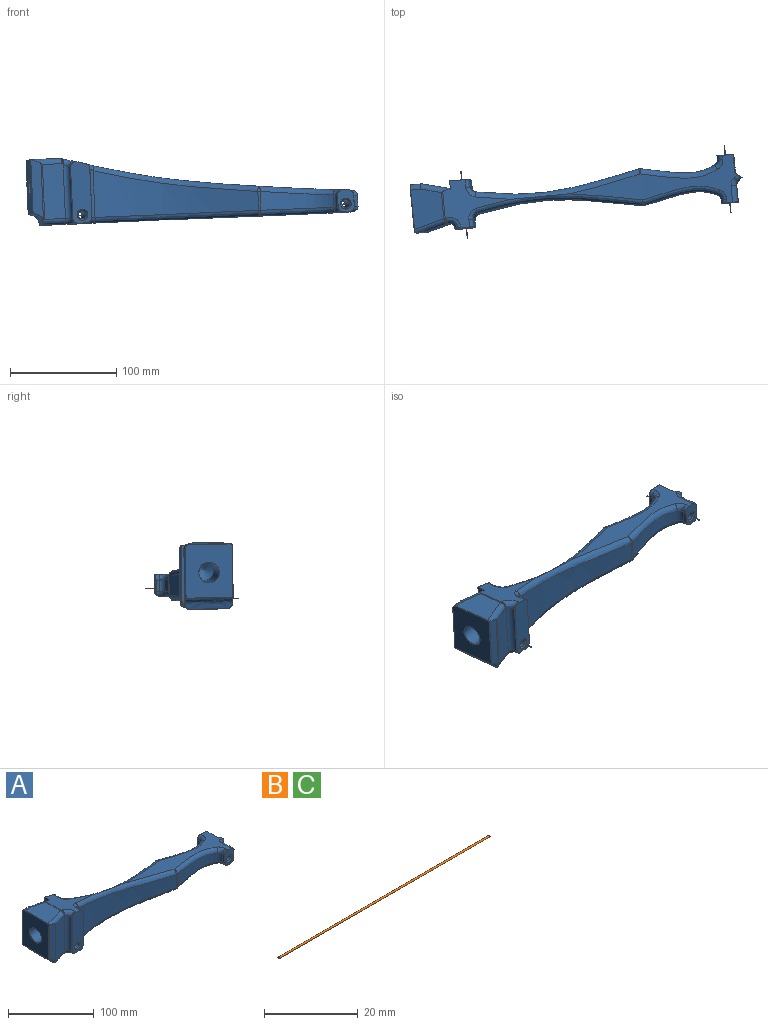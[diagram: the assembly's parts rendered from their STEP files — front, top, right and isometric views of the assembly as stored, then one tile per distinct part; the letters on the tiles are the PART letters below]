
ASSEMBLY  parts=3 mates=2
PART A: 137 faces, bbox 318.6x51.8x64.5 mm
  f0: bspline ~248.2x45mm, area 2358.8mm2, adj f35,f36,f41,f49,f51,f52,f54,f111
  f1: plane 155.5x39.82mm, normal (0,0,-1), area 2133.1mm2, adj f37,f46,f47,f48,f58,f92,f93,f94
  f2: plane 58.05x18.06mm, normal (0,-1,0), area 926.9mm2, adj f61,f62,f63,f64,f65,f66,f67,f68
  f3: plane 80.69x39.82mm, normal (0,0,-1), area 1452.2mm2, adj f37,f38,f40,f61,f74,f76,f77,f88
  f4: bspline ~218.34x45mm, area 1106.4mm2, adj f23,f41,f43,f44,f65,f70,f71,f73
  f5: plane 16.03x15.25mm, normal (0,1,0), area 166.9mm2, adj f96,f126,f128,f129,f130,f131
  f6: plane 54.56x18.06mm, normal (0,1,0), area 871.4mm2, adj f101,f120,f122,f123,f124,f125
  f7: plane 21.01x15.25mm, normal (0,-1,0), area 214.8mm2, adj f54,f55,f56,f57,f58,f59,f60,f92
  f8: plane 37.4x28.54mm, normal (0,0,1), area 908.9mm2, adj f69,f79,f104,f105,f106
  f9: cylinder r=3.81mm len=42.08mm, axis (0,-1,0), area 1007.3mm2, adj f17,f20
  f10: cylinder r=3.81mm len=42.08mm, axis (0,-1,0), area 1007.3mm2, adj f18,f19
  f11: plane 53.23x10.41mm, normal (0,1,0), area 486.4mm2, adj f24,f81,f86,f103,f104
  f12: plane 58.09x10.51mm, normal (0,-1,0), area 482.5mm2, adj f69,f72,f80,f83,f87
  f13: plane 50.31x44.32mm, normal (-1,0,0), area 1921.5mm2, adj f79,f80,f81,f82,f83,f91,f104
  f14: bspline ~45x11mm, area 707.6mm2, adj f82,f86,f87,f88,f89,f90,f103
  f15: cylinder r=9.5mm len=50.46mm, axis (-1,0,0), area 3011.8mm2, adj f16,f91
  f16: cone r=0mm half-angle=59deg, axis (-1,0,0), area 330.8mm2, adj f15
  f17: cone r=3.81mm half-angle=41deg, axis (0,-1,0), area 52.6mm2, adj f9,f67
  f18: cone r=3.81mm half-angle=41deg, axis (0,-1,0), area 52.6mm2, adj f10,f60
  f19: cone r=3.81mm half-angle=41deg, axis (0,1,0), area 52.6mm2, adj f10,f126,f127
  f20: cone r=3.81mm half-angle=41deg, axis (0,1,0), area 52.6mm2, adj f9,f120,f121
  f21: extruded ~51.76x20.1mm, area 1076.1mm2, adj f69,f70,f72,f74,f75
  f22: plane 48.1x0.5mm, normal (-1,0,0), area 24.2mm2, adj f63,f71,f75,f77
  f23: plane 54.85x8.17mm, normal (-1,0,0), area 385.9mm2, adj f4,f24,f102,f105,f122
  f24: extruded ~51.76x27.1mm, area 1450.4mm2, adj f11,f23,f103,f105
  f25: plane 46x7.21mm, normal (1,0,0), area 331.8mm2, adj f38,f42,f44,f64
  f26: extruded ~154.35x43.95mm, area 4768mm2, adj f37,f39,f41,f42
  f27: extruded ~69.57x17.76mm, area 1035.7mm2, adj f39,f47,f50,f52
  f28: plane 11.05x3.47mm, normal (-1,0,0), area 38.4mm2, adj f46,f49,f50,f57
  f29: plane 15.19x10.65mm, normal (1,0,0), area 161.8mm2, adj f56,f92,f133,f134
  f30: extruded ~10.37x3.88mm, area 52.3mm2, adj f35,f93,f133,f136
  f31: plane 46x7.21mm, normal (1,0,0), area 331.8mm2, adj f100,f110,f113,f124
  f32: plane 11.05x3.47mm, normal (-1,0,0), area 38.4mm2, adj f97,f115,f116,f129
  f33: extruded ~69.57x17.76mm, area 1035.7mm2, adj f98,f109,f115,f118
  f34: extruded ~154.35x43.95mm, area 4768mm2, adj f99,f109,f110,f111
  f35: extruded ~15.35x5.67mm, area 107.8mm2, adj f0,f30,f36,f94,f136
  f36: plane 17.55x15.35mm, normal (1,0,0), area 269.5mm2, adj f0,f35,f95,f128
  f37: bspline ~170.16x20.03mm, area 1250.7mm2, adj f1,f3,f26,f40,f45,f99
  f38: cylinder r=5.08mm len=7.21mm, axis (0,-1,0), area 57.6mm2, adj f3,f25,f40,f62
  f39: cylinder r=5.08mm len=17.76mm, axis (0,0,-1), area 38mm2, adj f26,f27,f45,f53
  f40: torus R=10.16mm, axis (0,0,-1), area 75.5mm2, adj f3,f37,f38,f42
  f41: bspline ~174.65x35.63mm, area 1266.6mm2, adj f0,f4,f26,f43,f53,f111
  f42: cylinder r=5.08mm len=46mm, axis (0,0,-1), area 312.2mm2, adj f25,f26,f40,f43
  f43: bspline ~12.37x10mm, area 70.4mm2, adj f4,f41,f42,f44
  f44: cylinder r=5.08mm len=7.21mm, axis (0,-1,0), area 48.4mm2, adj f4,f25,f43,f66
  f45: sphere r=5.08mm, area 10.9mm2, adj f37,f39,f47
  f46: cylinder r=5.08mm len=5.08mm, axis (0,1,0), area 27.7mm2, adj f1,f28,f48,f59
  f47: bspline ~91.6x17.35mm, area 577.7mm2, adj f1,f27,f45,f48
  f48: torus R=10.16mm, axis (0,0,-1), area 62.8mm2, adj f1,f46,f47,f50
  f49: cylinder r=5.08mm len=5.47mm, axis (0,-1,0), area 29mm2, adj f0,f28,f51,f55
  f50: cylinder r=5.08mm len=11.51mm, axis (0,0,-1), area 65.1mm2, adj f27,f28,f48,f51
  f51: bspline ~10.97x9.51mm, area 64.7mm2, adj f0,f49,f50,f52
  f52: bspline ~104.04x20.04mm, area 577.6mm2, adj f0,f27,f51,f53
  f53: sphere r=5.08mm, area 10.8mm2, adj f39,f41,f52
  f54: bspline ~44.88x3.6mm, area 0.9mm2, adj f0,f7,f55,f134
  f55: torus R=4.98mm, axis (0,-1,0), area 1.3mm2, adj f7,f49,f54,f57
  f56: cylinder r=0.1mm len=12.66mm, axis (0,0,1), area 1.9mm2, adj f7,f29,f92,f134
  f57: cylinder r=0.1mm len=11.05mm, axis (0,0,-1), area 1.8mm2, adj f7,f28,f55,f59
  f58: cylinder r=0.1mm len=6.3mm, axis (1,0,0), area 0.9mm2, adj f1,f7,f59,f92
  f59: torus R=4.98mm, axis (0,-1,0), area 1.3mm2, adj f7,f46,f57,f58
  f60: torus R=5.13mm, axis (0,-1,0), area 2.8mm2, adj f7,f18
  f61: cylinder r=0.1mm len=8.1mm, axis (1,0,0), area 1.3mm2, adj f2,f3,f62,f78
  f62: torus R=4.98mm, axis (0,-1,0), area 1.3mm2, adj f2,f38,f61,f64
  f63: cylinder r=0.1mm len=48.1mm, axis (0,0,1), area 7.6mm2, adj f2,f22,f68,f78
  f64: cylinder r=0.1mm len=46mm, axis (0,0,1), area 7.3mm2, adj f2,f25,f62,f66
  f65: bspline ~43.72x11.02mm, area 1.3mm2, adj f2,f4,f66,f68
  f66: torus R=4.98mm, axis (0,-1,0), area 1.1mm2, adj f2,f44,f64,f65
  f67: torus R=5.13mm, axis (0,-1,0), area 2.8mm2, adj f2,f17
  f68: torus R=4.98mm, axis (0,-1,0), area 1.5mm2, adj f2,f63,f65,f71
  f69: bspline ~45.01x16.53mm, area 208.1mm2, adj f8,f12,f21,f72,f80,f107
  f70: bspline ~8.19x6.81mm, area 8.8mm2, adj f4,f21,f73,f107
  f71: cylinder r=5.08mm len=6.37mm, axis (0,-1,0), area 4.7mm2, adj f4,f22,f68,f73
  f72: cylinder r=5.08mm len=54.28mm, axis (0,0,-1), area 71.1mm2, adj f12,f21,f69,f74,f89,f90
  f73: bspline ~14.84x11.45mm, area 110.3mm2, adj f4,f70,f71,f75
  f74: bspline ~39.2x14.85mm, area 167.5mm2, adj f3,f21,f72,f76,f90
  f75: cylinder r=5.08mm len=51.46mm, axis (0,0,-1), area 461.2mm2, adj f21,f22,f73,f76
  f76: torus R=10.16mm, axis (0,0,-1), area 100.8mm2, adj f3,f74,f75,f77
  f77: cylinder r=5.08mm len=5.08mm, axis (0,1,0), area 4mm2, adj f3,f22,f76,f78
  f78: torus R=4.98mm, axis (0,-1,0), area 1.3mm2, adj f2,f61,f63,f77
  f79: cylinder r=0.34mm len=39.23mm, axis (0,-1,0), area 20.6mm2, adj f8,f13,f80,f104
  f80: bspline ~3.21x1.11mm, area 1.4mm2, adj f12,f13,f69,f79,f83
  f81: cylinder r=0.34mm len=47.4mm, axis (0,0,1), area 25mm2, adj f11,f13,f84,f104
  f82: cylinder r=0.34mm len=44.31mm, axis (0,-1,0), area 20.1mm2, adj f13,f14,f84,f85
  f83: cylinder r=0.34mm len=50.02mm, axis (0,0,-1), area 26.9mm2, adj f12,f13,f80,f85
  f84: sphere r=0.34mm, area 0.1mm2, adj f81,f82,f86
  f85: sphere r=0.34mm, area 0.1mm2, adj f82,f83,f87
  f86: bspline ~10.62x9.04mm, area 7.1mm2, adj f11,f14,f84,f103
  f87: bspline ~15x9.6mm, area 6.6mm2, adj f12,f14,f85,f89
  f88: cylinder r=0.34mm len=36.12mm, axis (0,-1,0), area 16.5mm2, adj f3,f14,f90,f103
  f89: bspline ~2.54x1.12mm, area 0.2mm2, adj f14,f72,f87,f90
  f90: bspline ~6.32x4.56mm, area 3.7mm2, adj f14,f72,f74,f88,f89
  f91: torus R=9.84mm, axis (-1,0,0), area 32.6mm2, adj f13,f15
  f92: cylinder r=5.08mm len=20.05mm, axis (0,-1,0), area 135.7mm2, adj f1,f7,f29,f56,f58,f132
  f93: bspline ~13.63x12.67mm, area 35.9mm2, adj f1,f30,f94,f132
  f94: bspline ~13.63x12.67mm, area 45.2mm2, adj f1,f35,f93,f95
  f95: cylinder r=5.08mm len=20.02mm, axis (0,-1,0), area 133.1mm2, adj f1,f36,f94,f96,f128
  f96: cylinder r=5.08mm len=15.39mm, axis (-1,0,0), area 81mm2, adj f1,f5,f95,f97,f127,f128,f129
  f97: cylinder r=5.08mm len=9.96mm, axis (0,1,0), area 32.4mm2, adj f1,f32,f96,f114,f129
  f98: bspline ~90.96x17.6mm, area 601mm2, adj f1,f33,f99,f109,f114
  f99: bspline ~181.69x20.03mm, area 1221.2mm2, adj f1,f3,f34,f37,f98,f108,f109
  f100: cylinder r=5.08mm len=15.48mm, axis (0,-1,0), area 67.5mm2, adj f3,f31,f101,f108,f124
  f101: cylinder r=5.08mm len=18.2mm, axis (-1,0,0), area 103.4mm2, adj f3,f6,f100,f102,f121,f122,f124
  f102: cylinder r=5.08mm len=13.59mm, axis (0,1,0), area 61mm2, adj f3,f23,f101,f103,f122
  f103: bspline ~54.46x18.31mm, area 240.9mm2, adj f3,f11,f14,f24,f86,f88,f102
  f104: cylinder r=5.08mm len=10.49mm, axis (1,0,0), area 80.4mm2, adj f8,f11,f13,f79,f81,f105
  f105: bspline ~40.57x15.23mm, area 200.8mm2, adj f4,f8,f23,f24,f104,f106
  f106: cylinder r=5.08mm len=25.7mm, axis (0,-1,0), area 33.6mm2, adj f4,f8,f105,f107
  f107: sphere r=5.08mm, area 6.4mm2, adj f69,f70,f106
  f108: bspline ~9.13x8.2mm, area 24.2mm2, adj f99,f100,f110
  f109: cylinder r=5.08mm len=18.82mm, axis (0,0,-1), area 39.2mm2, adj f33,f34,f98,f99,f119
  f110: cylinder r=5.08mm len=46mm, axis (0,0,-1), area 312.2mm2, adj f31,f34,f108,f112
  f111: bspline ~174.65x35.63mm, area 1266.6mm2, adj f0,f4,f34,f41,f112,f119
  f112: bspline ~10.74x10.5mm, area 70.4mm2, adj f4,f110,f111,f113
  f113: cylinder r=5.08mm len=7.21mm, axis (0,-1,0), area 48.4mm2, adj f4,f31,f112,f125
  f114: bspline ~8.02x6.42mm, area 19.4mm2, adj f97,f98,f115
  f115: cylinder r=5.08mm len=11.51mm, axis (0,0,-1), area 65.1mm2, adj f32,f33,f114,f117
  f116: cylinder r=5.08mm len=5.47mm, axis (0,-1,0), area 29mm2, adj f0,f32,f117,f131
  f117: bspline ~11.85x8.87mm, area 64.7mm2, adj f0,f115,f116,f118
  f118: bspline ~104.04x20.03mm, area 577.6mm2, adj f0,f33,f117,f119
  f119: sphere r=5.08mm, area 10.8mm2, adj f109,f111,f118
  f120: torus R=5.13mm, axis (0,-1,0), area 1.9mm2, adj f6,f20,f121
  f121: bspline ~9.13x2.56mm, area 1.1mm2, adj f20,f101,f120
  f122: cylinder r=0.1mm len=55.24mm, axis (0,0,1), area 8.7mm2, adj f6,f23,f101,f102,f123
  f123: bspline ~48.61x12.33mm, area 2.4mm2, adj f4,f6,f122,f125
  f124: cylinder r=0.1mm len=46.55mm, axis (0,0,1), area 7.3mm2, adj f6,f31,f100,f101,f125
  f125: torus R=4.98mm, axis (0,-1,0), area 1.1mm2, adj f6,f113,f123,f124
  f126: torus R=5.13mm, axis (0,-1,0), area 1.9mm2, adj f5,f19,f127
  f127: bspline ~9.13x2.56mm, area 1.1mm2, adj f19,f96,f126
  f128: cylinder r=0.1mm len=15.9mm, axis (0,0,1), area 2.5mm2, adj f5,f36,f95,f96,f130
  f129: cylinder r=0.1mm len=11.6mm, axis (0,0,-1), area 1.8mm2, adj f5,f32,f96,f97,f131
  f130: bspline ~44.88x3.6mm, area 1.6mm2, adj f0,f5,f128,f131
  f131: torus R=4.98mm, axis (0,-1,0), area 1.3mm2, adj f5,f116,f129,f130
  f132: bspline ~6.87x6.14mm, area 14.6mm2, adj f92,f93,f133
  f133: cylinder r=5.08mm len=10.65mm, axis (0,0,-1), area 46.2mm2, adj f29,f30,f132,f135
  f134: cylinder r=5.08mm len=15.29mm, axis (0,-1,0), area 116mm2, adj f0,f7,f29,f54,f56,f135
  f135: bspline ~10.85x7.33mm, area 46.4mm2, adj f0,f133,f134,f136
  f136: bspline ~14.85x13.86mm, area 35.6mm2, adj f0,f30,f35,f135
PART B: 3 faces, bbox 63.5x0.4x0.4 mm
  f0: plane 0.41x0.41mm, normal (-1,0,0), area 0.1mm2, adj f2
  f1: plane 0.41x0.41mm, normal (1,0,0), area 0.1mm2, adj f2
  f2: cylinder r=0.2mm len=63.5mm, axis (1,0,0), area 81.1mm2, adj f0,f1
PART C: same geometry as B
PLACE A rot(axis=(-0.16,-0.4,0.9),6.1deg) t=(-33.29,116.29,-93.14)mm
PLACE B rot(axis=(0.02,-0.04,-1),84.5deg) t=(242.63,150.9,-152.03)mm
PLACE C rot(axis=(0.02,-0.04,-1),84.5deg) t=(-5.46,126.84,-162.55)mm
MATE cylindrical C.f2 <-> A.f9  axis (0.1,-1,0.02) through (0.65,63.65,-161.32)mm
MATE cylindrical B.f2 <-> A.f10  axis (-0.1,1,-0.02) through (242.63,150.9,-152.03)mm
